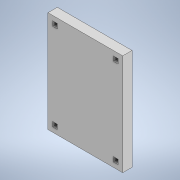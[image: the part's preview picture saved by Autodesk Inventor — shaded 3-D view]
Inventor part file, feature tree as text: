
AUTODESK INVENTOR PART (.ipt)
format: ipt  version: 2020.2 (Build 242310000, 310)  size: 208,384 bytes
history: native  units: mm
features: extrude x3, sketch x3, fillet x1
ambient origin geometry x8: Origin, YZ Plane, XZ Plane, XY Plane, X Axis, Y Axis, Z Axis, Center Point
bodies: Solide1 (feature_tree)
feature tree (7):
  extrude  "Extrusion1"  Depth=48.0mm
  extrude  "Extrusion2"  Depth=65.0mm
  extrude  "Extrusion4"  Depth=6.0mm TaperAngle=0.0deg
  fillet  "Congé2"  Radius=3.0mm
  sketch  "Esquisse1"
  sketch  "Esquisse2"
  sketch  "Esquisse4"
